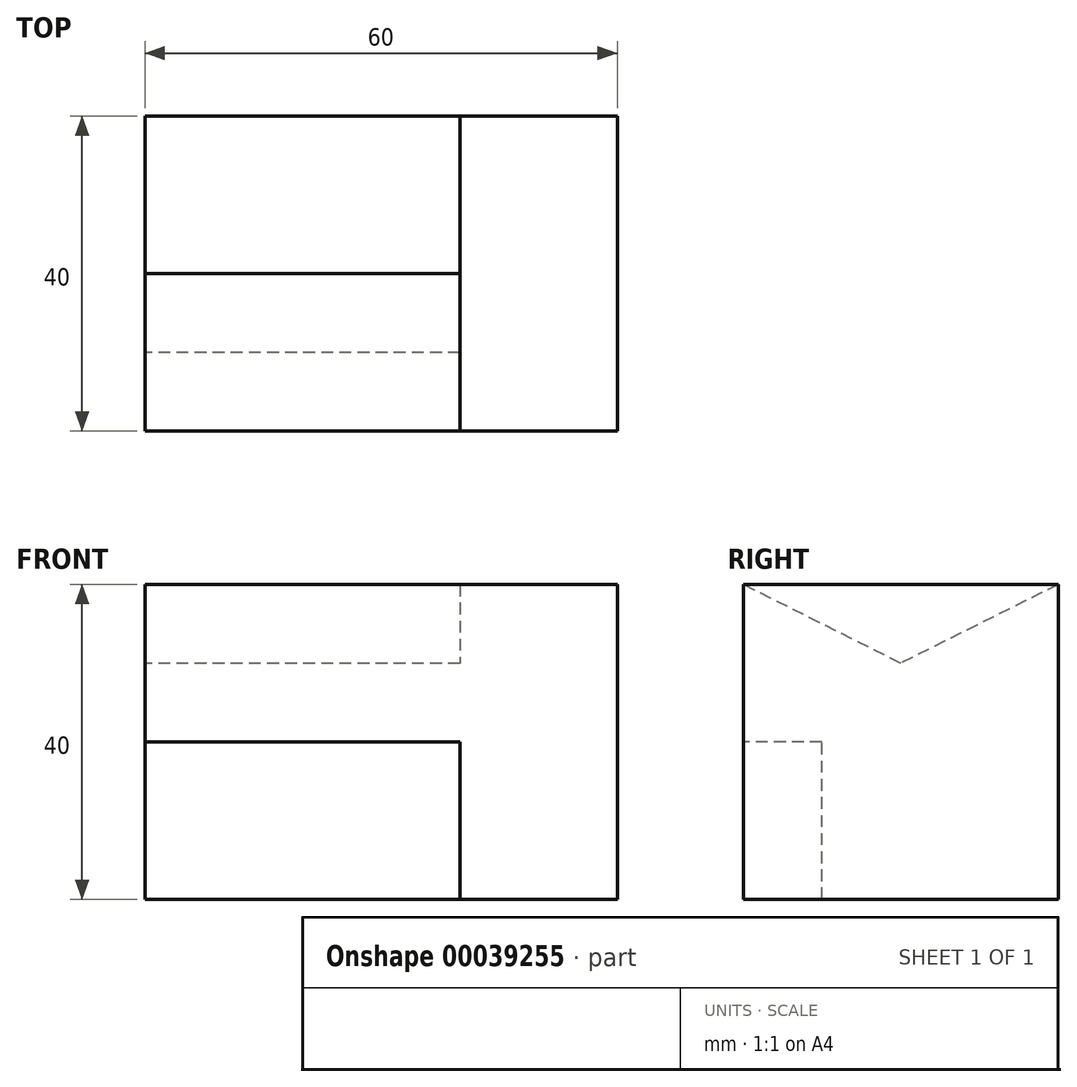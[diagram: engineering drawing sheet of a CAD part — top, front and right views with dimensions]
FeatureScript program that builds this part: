
annotation { "Feature Type Name" : "Feature", "Feature Type Description" : "" }
export const myFeature = defineFeature(function(context is Context, id is Id, definition is map)
    precondition{}
    {
        {
            var Q0;
            Q0=qCreatedBy(makeId("Front.planeOp"),FACE);
            var sketch = newSketch(context, id + "F0", { "sketchPlane" : qUnion([Q0])});
            skLineSegment(sketch, "E0.bottom", {"start": v(-37.39, 34.63) * mm, "end": v(22.61, 34.63) * mm});
            skLineSegment(sketch, "E0.top", {"start": v(-37.39, -5.37) * mm, "end": v(22.61, -5.37) * mm});
            skLineSegment(sketch, "E0.left", {"start": v(-37.39, 34.63) * mm, "end": v(-37.39, -5.37) * mm});
            skLineSegment(sketch, "E0.right", {"start": v(22.61, 34.63) * mm, "end": v(22.61, -5.37) * mm});
            skSolve(sketch);
        }
        {
            var Q0;
            Q0=makeQuery(id+"F0.imprint","IMPRINT",FACE,{"disambiguationData":[TD([[makeQuery(id+"F0.imprint","IMPRINT",EDGE,{"derivedFrom":sQuery(id+"F0.wireOp",EDGE,"E0.bottom")}),-1.0]])]});
            extrude(context, id + "F1", {"entities" : qUnion([Q0]), "depth" : 40 * mm});
        }
        {
            var Q0;
            Q0=makeQuery(id+"F1.opExtrude","SWEPT_FACE",FACE,{"disambiguationData":[OSD([sQuery(id+"F0.wireOp",EDGE,"E0.left")])]});
            var sketch = newSketch(context, id + "F2", { "sketchPlane" : qUnion([Q0])});
            skLineSegment(sketch, "E1.bottom", {"start": v(30, -5.37) * mm, "end": v(40, -5.37) * mm});
            skLineSegment(sketch, "E1.top", {"start": v(30, 14.63) * mm, "end": v(40, 14.63) * mm});
            skLineSegment(sketch, "E1.left", {"start": v(30, -5.37) * mm, "end": v(30, 14.63) * mm});
            skLineSegment(sketch, "E1.right", {"start": v(40, -5.37) * mm, "end": v(40, 14.63) * mm});
            skSolve(sketch);
        }
        {
            var Q0;
            Q0=makeQuery(id+"F2.imprint","IMPRINT",FACE,{"disambiguationData":[TD([[makeQuery(id+"F2.imprint","IMPRINT",EDGE,{"derivedFrom":sQuery(id+"F2.wireOp",EDGE,"E1.bottom")}),-1.0]])]});
            extrude(context, id + "F3", {"entities" : qUnion([Q0]), "operationType" : NewBodyOperationType.REMOVE, "oppositeDirection" : true, "depth" : 40 * mm});
        }
        {
            var Q0;
            Q0=makeQuery(id+"F1.opExtrude","SWEPT_FACE",FACE,{"disambiguationData":[OSD([sQuery(id+"F0.wireOp",EDGE,"E0.left")])]});
            var sketch = newSketch(context, id + "F4", { "sketchPlane" : qUnion([Q0])});
            skLineSegment(sketch, "E2", {"start": v(0, 34.63) * mm, "end": v(20, 24.63) * mm});
            skPoint(sketch, "E2.endSnap0", {"position": v(20, 34.63) * mm});
            skLineSegment(sketch, "E3", {"start": v(20, 24.63) * mm, "end": v(40, 34.63) * mm});
            skSolve(sketch);
        }
        {
            var Q0;
            Q0=makeQuery(id+"F4.imprint","IMPRINT",FACE,{"disambiguationData":[TD([[makeQuery(id+"F4.imprint","IMPRINT",EDGE,{"derivedFrom":sQuery(id+"F4.wireOp",EDGE,"E2")}),1.0]])]});
            extrude(context, id + "F5", {"entities" : qUnion([Q0]), "operationType" : NewBodyOperationType.REMOVE, "oppositeDirection" : true, "depth" : 40 * mm});
        }
    });
